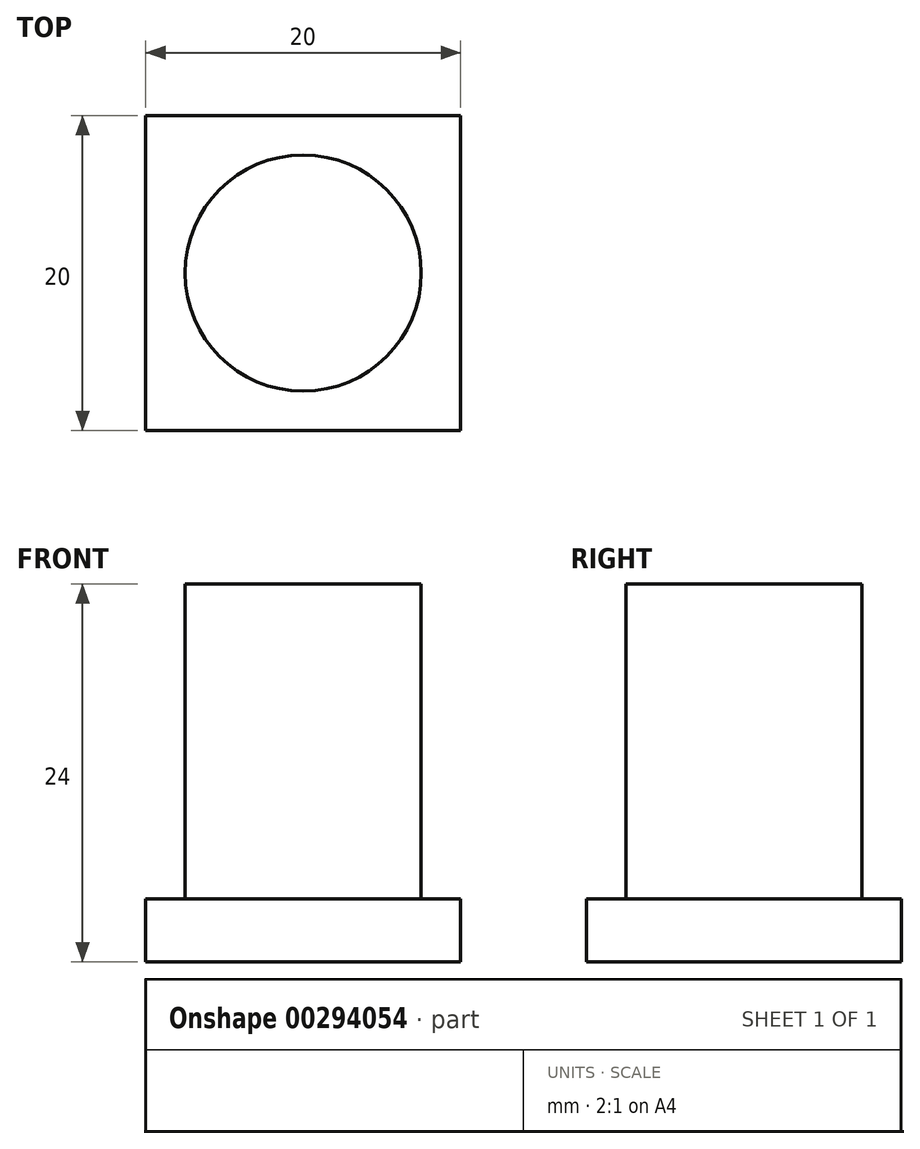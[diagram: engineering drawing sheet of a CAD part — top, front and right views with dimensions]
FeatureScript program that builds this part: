
annotation { "Feature Type Name" : "Feature", "Feature Type Description" : "" }
export const myFeature = defineFeature(function(context is Context, id is Id, definition is map)
    precondition{}
    {
        {
            var Q0;
            Q0=qCreatedBy(makeId("Top.planeOp"),FACE);
            var sketch = newSketch(context, id + "F0", { "sketchPlane" : qUnion([Q0])});
            skLineSegment(sketch, "E0.bottom", {"start": v(-10, 10) * mm, "end": v(10, 10) * mm});
            skLineSegment(sketch, "E0.top", {"start": v(-10, -10) * mm, "end": v(10, -10) * mm});
            skLineSegment(sketch, "E0.left", {"start": v(-10, 10) * mm, "end": v(-10, -10) * mm});
            skLineSegment(sketch, "E0.right", {"start": v(10, 10) * mm, "end": v(10, -10) * mm});
            skPoint(sketch, "E0.middle", {"position": v(0, 0) * mm});
            skSolve(sketch);
        }
        {
            var Q0;
            Q0=makeQuery(id+"F0.imprint","IMPRINT",FACE,{"disambiguationData":[TD([[makeQuery(id+"F0.imprint","IMPRINT",EDGE,{"derivedFrom":sQuery(id+"F0.wireOp",EDGE,"E0.bottom")}),-1.0]])]});
            extrude(context, id + "F1", {"entities" : qUnion([Q0]), "depth" : 4 * mm});
        }
        {
            var Q0;
            Q0=makeQuery(id+"F1.opExtrude","CAP_FACE",FACE,{"disambiguationData":[OSD([sQuery(id+"F0.wireOp",EDGE,"E0.bottom"),sQuery(id+"F0.wireOp",EDGE,"E0.top"),sQuery(id+"F0.wireOp",EDGE,"E0.left"),sQuery(id+"F0.wireOp",EDGE,"E0.right")])],"isStart":false});
            var sketch = newSketch(context, id + "F2", { "sketchPlane" : qUnion([Q0])});
            skCircle(sketch, "E1", {"center": v(0, 0) * mm, "radius": 7.5 * mm});
            skSolve(sketch);
        }
        {
            var Q0;
            Q0 = qSketchRegion(id + "F2", true);
            extrude(context, id + "F3", {"entities" : qUnion([Q0]), "operationType" : NewBodyOperationType.ADD, "depth" : 20 * mm});
        }
    });
